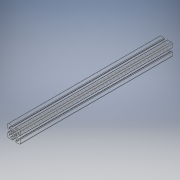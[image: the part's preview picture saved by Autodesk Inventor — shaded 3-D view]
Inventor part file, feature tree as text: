
AUTODESK INVENTOR PART (.ipt)
format: ipt  version: 2019 (Build 230136000, 136)  size: 233,984 bytes
history: native  units: in
note: dims shown in document units (in); Inventor stores cm internally (conversion verified against a paired STEP export)
features: extrude x1, sketch x1
ambient origin geometry x8: Origin, YZ Plane, XZ Plane, XY Plane, X Axis, Y Axis, Z Axis, Center Point
bodies: Solid1 (feature_tree)
feature tree (2):
  extrude  "Extrusion1"  [1 undecoded]
  sketch  "Sketch1"  dims[d0=18.0in d1=0.0in]
note: 1 required parameter value undecoded (feature->parameter linkage not recoverable at this tier; creation-order binding heuristic only, values carry confidence <= 0.55)
